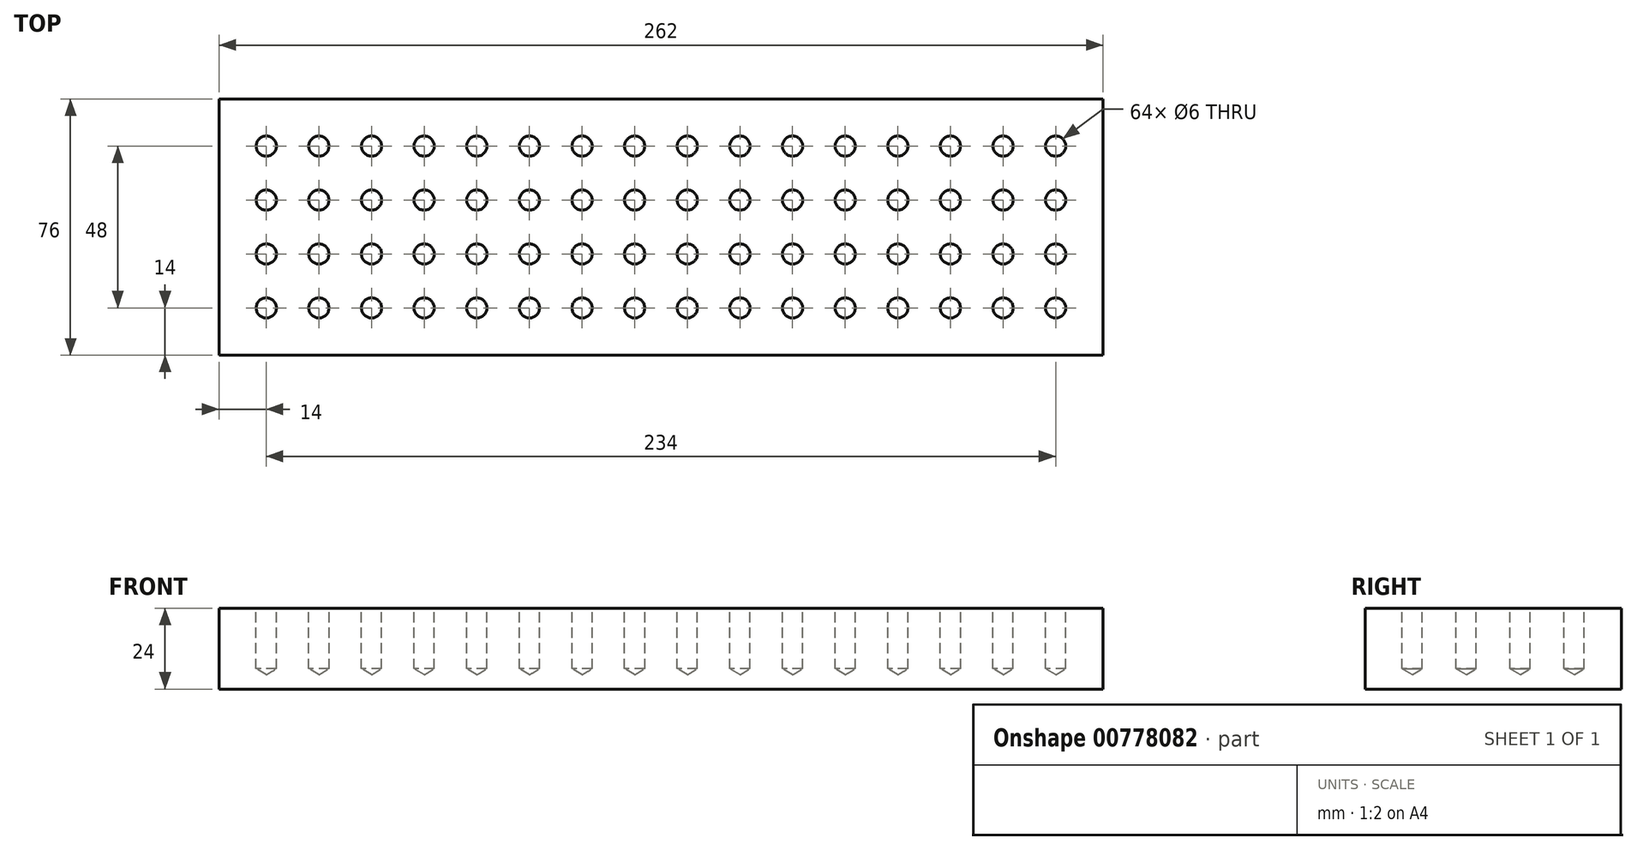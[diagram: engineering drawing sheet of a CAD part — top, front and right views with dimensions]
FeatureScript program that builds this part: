
annotation { "Feature Type Name" : "Feature", "Feature Type Description" : "" }
export const myFeature = defineFeature(function(context is Context, id is Id, definition is map)
    precondition{}
    {
        {
            var Q0;
            Q0=qCreatedBy(makeId("Top.planeOp"),FACE);
            var sketch = newSketch(context, id + "F0", { "sketchPlane" : qUnion([Q0])});
            skLineSegment(sketch, "E0.bottom", {"start": v(-131, 38) * mm, "end": v(131, 38) * mm});
            skLineSegment(sketch, "E0.top", {"start": v(-131, -38) * mm, "end": v(131, -38) * mm});
            skLineSegment(sketch, "E0.left", {"start": v(-131, 38) * mm, "end": v(-131, -38) * mm});
            skLineSegment(sketch, "E0.right", {"start": v(131, 38) * mm, "end": v(131, -38) * mm});
            skPoint(sketch, "E1", {"position": v(-131, 0) * mm});
            skPoint(sketch, "E2", {"position": v(0, 38) * mm});
            skPoint(sketch, "E3", {"position": v(-117, -24) * mm});
            skPoint(sketch, "E4.0.1.0", {"position": v(-117, -8) * mm});
            skPoint(sketch, "E4.0.2.0", {"position": v(-117, 8) * mm});
            skPoint(sketch, "E4.0.3.0", {"position": v(-117, 24) * mm});
            skPoint(sketch, "E4.1.0.0", {"position": v(-101.4, -24) * mm});
            skPoint(sketch, "E4.1.1.0", {"position": v(-101.4, -8) * mm});
            skPoint(sketch, "E4.1.2.0", {"position": v(-101.4, 8) * mm});
            skPoint(sketch, "E4.1.3.0", {"position": v(-101.4, 24) * mm});
            skPoint(sketch, "E4.2.0.0", {"position": v(-85.8, -24) * mm});
            skPoint(sketch, "E4.2.1.0", {"position": v(-85.8, -8) * mm});
            skPoint(sketch, "E4.2.2.0", {"position": v(-85.8, 8) * mm});
            skPoint(sketch, "E4.2.3.0", {"position": v(-85.8, 24) * mm});
            skPoint(sketch, "E4.3.0.0", {"position": v(-70.2, -24) * mm});
            skPoint(sketch, "E4.3.1.0", {"position": v(-70.2, -8) * mm});
            skPoint(sketch, "E4.3.2.0", {"position": v(-70.2, 8) * mm});
            skPoint(sketch, "E4.3.3.0", {"position": v(-70.2, 24) * mm});
            skPoint(sketch, "E4.4.0.0", {"position": v(-54.6, -24) * mm});
            skPoint(sketch, "E4.4.1.0", {"position": v(-54.6, -8) * mm});
            skPoint(sketch, "E4.4.2.0", {"position": v(-54.6, 8) * mm});
            skPoint(sketch, "E4.4.3.0", {"position": v(-54.6, 24) * mm});
            skPoint(sketch, "E4.5.0.0", {"position": v(-39, -24) * mm});
            skPoint(sketch, "E4.5.1.0", {"position": v(-39, -8) * mm});
            skPoint(sketch, "E4.5.2.0", {"position": v(-39, 8) * mm});
            skPoint(sketch, "E4.5.3.0", {"position": v(-39, 24) * mm});
            skPoint(sketch, "E4.6.0.0", {"position": v(-23.4, -24) * mm});
            skPoint(sketch, "E4.6.1.0", {"position": v(-23.4, -8) * mm});
            skPoint(sketch, "E4.6.2.0", {"position": v(-23.4, 8) * mm});
            skPoint(sketch, "E4.6.3.0", {"position": v(-23.4, 24) * mm});
            skPoint(sketch, "E4.7.0.0", {"position": v(-7.8, -24) * mm});
            skPoint(sketch, "E4.7.1.0", {"position": v(-7.8, -8) * mm});
            skPoint(sketch, "E4.7.2.0", {"position": v(-7.8, 8) * mm});
            skPoint(sketch, "E4.7.3.0", {"position": v(-7.8, 24) * mm});
            skPoint(sketch, "E4.8.0.0", {"position": v(7.8, -24) * mm});
            skPoint(sketch, "E4.8.1.0", {"position": v(7.8, -8) * mm});
            skPoint(sketch, "E4.8.2.0", {"position": v(7.8, 8) * mm});
            skPoint(sketch, "E4.8.3.0", {"position": v(7.8, 24) * mm});
            skPoint(sketch, "E4.9.0.0", {"position": v(23.4, -24) * mm});
            skPoint(sketch, "E4.9.1.0", {"position": v(23.4, -8) * mm});
            skPoint(sketch, "E4.9.2.0", {"position": v(23.4, 8) * mm});
            skPoint(sketch, "E4.9.3.0", {"position": v(23.4, 24) * mm});
            skPoint(sketch, "E4.10.0.0", {"position": v(39, -24) * mm});
            skPoint(sketch, "E4.10.1.0", {"position": v(39, -8) * mm});
            skPoint(sketch, "E4.10.2.0", {"position": v(39, 8) * mm});
            skPoint(sketch, "E4.10.3.0", {"position": v(39, 24) * mm});
            skPoint(sketch, "E4.11.0.0", {"position": v(54.6, -24) * mm});
            skPoint(sketch, "E4.11.1.0", {"position": v(54.6, -8) * mm});
            skPoint(sketch, "E4.11.2.0", {"position": v(54.6, 8) * mm});
            skPoint(sketch, "E4.11.3.0", {"position": v(54.6, 24) * mm});
            skPoint(sketch, "E4.12.0.0", {"position": v(70.2, -24) * mm});
            skPoint(sketch, "E4.12.1.0", {"position": v(70.2, -8) * mm});
            skPoint(sketch, "E4.12.2.0", {"position": v(70.2, 8) * mm});
            skPoint(sketch, "E4.12.3.0", {"position": v(70.2, 24) * mm});
            skLineSegment(sketch, "E4.direction1", {"start": v(-117, -24) * mm, "end": v(-101.4, -24) * mm, "construction": true});
            skLineSegment(sketch, "E4.direction2", {"start": v(-117, -24) * mm, "end": v(-117, -8) * mm, "construction": true});
            skPoint(sketch, "E5.0.13.0", {"position": v(85.8, -24) * mm});
            skPoint(sketch, "E5.0.13.1", {"position": v(85.8, -8) * mm});
            skPoint(sketch, "E5.0.13.2", {"position": v(85.8, 8) * mm});
            skPoint(sketch, "E5.0.13.3", {"position": v(85.8, 24) * mm});
            skPoint(sketch, "E5.0.14.0", {"position": v(101.4, -24) * mm});
            skPoint(sketch, "E5.0.14.1", {"position": v(101.4, -8) * mm});
            skPoint(sketch, "E5.0.14.2", {"position": v(101.4, 8) * mm});
            skPoint(sketch, "E5.0.14.3", {"position": v(101.4, 24) * mm});
            skPoint(sketch, "E6.0.15.0", {"position": v(117, -24) * mm});
            skPoint(sketch, "E6.0.15.1", {"position": v(117, -8) * mm});
            skPoint(sketch, "E6.0.15.2", {"position": v(117, 8) * mm});
            skPoint(sketch, "E6.0.15.3", {"position": v(117, 24) * mm});
            skSolve(sketch);
        }
        {
            var Q0;
            Q0=makeQuery(id+"F0.imprint","IMPRINT",FACE,{"disambiguationData":[TD([[makeQuery(id+"F0.imprint","IMPRINT",EDGE,{"derivedFrom":sQuery(id+"F0.wireOp",EDGE,"E0.bottom")}),-1.0]])]});
            extrude(context, id + "F1", {"entities" : qUnion([Q0]), "depth" : 24 * mm, "offsetDistance" : 25 * mm});
        }
        {
            var Q0;
            Q0=makeQuery(id+"F1.opExtrude","CAP_FACE",FACE,{"disambiguationData":[OSD([sQuery(id+"F0.wireOp",EDGE,"E0.bottom"),sQuery(id+"F0.wireOp",EDGE,"E0.top"),sQuery(id+"F0.wireOp",EDGE,"E0.left"),sQuery(id+"F0.wireOp",EDGE,"E0.right")])],"isStart":false});
            var sketch = newSketch(context, id + "F2", { "sketchPlane" : qUnion([Q0])});
            skPoint(sketch, "E7", {"position": v(-117, -24) * mm});
            skCircle(sketch, "E8", {"center": v(-117, -24) * mm, "radius": 3 * mm});
            skCircle(sketch, "E9.0.1.0", {"center": v(-117, -8) * mm, "radius": 3 * mm});
            skPoint(sketch, "E9.0.1.1", {"position": v(-117, -8) * mm});
            skCircle(sketch, "E9.0.2.0", {"center": v(-117, 8) * mm, "radius": 3 * mm});
            skPoint(sketch, "E9.0.2.1", {"position": v(-117, 8) * mm});
            skCircle(sketch, "E9.0.3.0", {"center": v(-117, 24) * mm, "radius": 3 * mm});
            skPoint(sketch, "E9.0.3.1", {"position": v(-117, 24) * mm});
            skCircle(sketch, "E9.1.0.0", {"center": v(-101.4, -24) * mm, "radius": 3 * mm});
            skPoint(sketch, "E9.1.0.1", {"position": v(-101.4, -24) * mm});
            skCircle(sketch, "E9.1.1.0", {"center": v(-101.4, -8) * mm, "radius": 3 * mm});
            skPoint(sketch, "E9.1.1.1", {"position": v(-101.4, -8) * mm});
            skCircle(sketch, "E9.1.2.0", {"center": v(-101.4, 8) * mm, "radius": 3 * mm});
            skPoint(sketch, "E9.1.2.1", {"position": v(-101.4, 8) * mm});
            skCircle(sketch, "E9.1.3.0", {"center": v(-101.4, 24) * mm, "radius": 3 * mm});
            skPoint(sketch, "E9.1.3.1", {"position": v(-101.4, 24) * mm});
            skCircle(sketch, "E9.2.0.0", {"center": v(-85.8, -24) * mm, "radius": 3 * mm});
            skPoint(sketch, "E9.2.0.1", {"position": v(-85.8, -24) * mm});
            skCircle(sketch, "E9.2.1.0", {"center": v(-85.8, -8) * mm, "radius": 3 * mm});
            skPoint(sketch, "E9.2.1.1", {"position": v(-85.8, -8) * mm});
            skCircle(sketch, "E9.2.2.0", {"center": v(-85.8, 8) * mm, "radius": 3 * mm});
            skPoint(sketch, "E9.2.2.1", {"position": v(-85.8, 8) * mm});
            skCircle(sketch, "E9.2.3.0", {"center": v(-85.8, 24) * mm, "radius": 3 * mm});
            skPoint(sketch, "E9.2.3.1", {"position": v(-85.8, 24) * mm});
            skCircle(sketch, "E9.3.0.0", {"center": v(-70.2, -24) * mm, "radius": 3 * mm});
            skPoint(sketch, "E9.3.0.1", {"position": v(-70.2, -24) * mm});
            skCircle(sketch, "E9.3.1.0", {"center": v(-70.2, -8) * mm, "radius": 3 * mm});
            skPoint(sketch, "E9.3.1.1", {"position": v(-70.2, -8) * mm});
            skCircle(sketch, "E9.3.2.0", {"center": v(-70.2, 8) * mm, "radius": 3 * mm});
            skPoint(sketch, "E9.3.2.1", {"position": v(-70.2, 8) * mm});
            skCircle(sketch, "E9.3.3.0", {"center": v(-70.2, 24) * mm, "radius": 3 * mm});
            skPoint(sketch, "E9.3.3.1", {"position": v(-70.2, 24) * mm});
            skCircle(sketch, "E9.4.0.0", {"center": v(-54.6, -24) * mm, "radius": 3 * mm});
            skPoint(sketch, "E9.4.0.1", {"position": v(-54.6, -24) * mm});
            skCircle(sketch, "E9.4.1.0", {"center": v(-54.6, -8) * mm, "radius": 3 * mm});
            skPoint(sketch, "E9.4.1.1", {"position": v(-54.6, -8) * mm});
            skCircle(sketch, "E9.4.2.0", {"center": v(-54.6, 8) * mm, "radius": 3 * mm});
            skPoint(sketch, "E9.4.2.1", {"position": v(-54.6, 8) * mm});
            skCircle(sketch, "E9.4.3.0", {"center": v(-54.6, 24) * mm, "radius": 3 * mm});
            skPoint(sketch, "E9.4.3.1", {"position": v(-54.6, 24) * mm});
            skCircle(sketch, "E9.5.0.0", {"center": v(-39, -24) * mm, "radius": 3 * mm});
            skPoint(sketch, "E9.5.0.1", {"position": v(-39, -24) * mm});
            skCircle(sketch, "E9.5.1.0", {"center": v(-39, -8) * mm, "radius": 3 * mm});
            skPoint(sketch, "E9.5.1.1", {"position": v(-39, -8) * mm});
            skCircle(sketch, "E9.5.2.0", {"center": v(-39, 8) * mm, "radius": 3 * mm});
            skPoint(sketch, "E9.5.2.1", {"position": v(-39, 8) * mm});
            skCircle(sketch, "E9.5.3.0", {"center": v(-39, 24) * mm, "radius": 3 * mm});
            skPoint(sketch, "E9.5.3.1", {"position": v(-39, 24) * mm});
            skCircle(sketch, "E9.6.0.0", {"center": v(-23.4, -24) * mm, "radius": 3 * mm});
            skPoint(sketch, "E9.6.0.1", {"position": v(-23.4, -24) * mm});
            skCircle(sketch, "E9.6.1.0", {"center": v(-23.4, -8) * mm, "radius": 3 * mm});
            skPoint(sketch, "E9.6.1.1", {"position": v(-23.4, -8) * mm});
            skCircle(sketch, "E9.6.2.0", {"center": v(-23.4, 8) * mm, "radius": 3 * mm});
            skPoint(sketch, "E9.6.2.1", {"position": v(-23.4, 8) * mm});
            skCircle(sketch, "E9.6.3.0", {"center": v(-23.4, 24) * mm, "radius": 3 * mm});
            skPoint(sketch, "E9.6.3.1", {"position": v(-23.4, 24) * mm});
            skCircle(sketch, "E9.7.0.0", {"center": v(-7.8, -24) * mm, "radius": 3 * mm});
            skPoint(sketch, "E9.7.0.1", {"position": v(-7.8, -24) * mm});
            skCircle(sketch, "E9.7.1.0", {"center": v(-7.8, -8) * mm, "radius": 3 * mm});
            skPoint(sketch, "E9.7.1.1", {"position": v(-7.8, -8) * mm});
            skCircle(sketch, "E9.7.2.0", {"center": v(-7.8, 8) * mm, "radius": 3 * mm});
            skPoint(sketch, "E9.7.2.1", {"position": v(-7.8, 8) * mm});
            skCircle(sketch, "E9.7.3.0", {"center": v(-7.8, 24) * mm, "radius": 3 * mm});
            skPoint(sketch, "E9.7.3.1", {"position": v(-7.8, 24) * mm});
            skCircle(sketch, "E9.8.0.0", {"center": v(7.8, -24) * mm, "radius": 3 * mm});
            skPoint(sketch, "E9.8.0.1", {"position": v(7.8, -24) * mm});
            skCircle(sketch, "E9.8.1.0", {"center": v(7.8, -8) * mm, "radius": 3 * mm});
            skPoint(sketch, "E9.8.1.1", {"position": v(7.8, -8) * mm});
            skCircle(sketch, "E9.8.2.0", {"center": v(7.8, 8) * mm, "radius": 3 * mm});
            skPoint(sketch, "E9.8.2.1", {"position": v(7.8, 8) * mm});
            skCircle(sketch, "E9.8.3.0", {"center": v(7.8, 24) * mm, "radius": 3 * mm});
            skPoint(sketch, "E9.8.3.1", {"position": v(7.8, 24) * mm});
            skCircle(sketch, "E9.9.0.0", {"center": v(23.4, -24) * mm, "radius": 3 * mm});
            skPoint(sketch, "E9.9.0.1", {"position": v(23.4, -24) * mm});
            skCircle(sketch, "E9.9.1.0", {"center": v(23.4, -8) * mm, "radius": 3 * mm});
            skPoint(sketch, "E9.9.1.1", {"position": v(23.4, -8) * mm});
            skCircle(sketch, "E9.9.2.0", {"center": v(23.4, 8) * mm, "radius": 3 * mm});
            skPoint(sketch, "E9.9.2.1", {"position": v(23.4, 8) * mm});
            skCircle(sketch, "E9.9.3.0", {"center": v(23.4, 24) * mm, "radius": 3 * mm});
            skPoint(sketch, "E9.9.3.1", {"position": v(23.4, 24) * mm});
            skCircle(sketch, "E9.10.0.0", {"center": v(39, -24) * mm, "radius": 3 * mm});
            skPoint(sketch, "E9.10.0.1", {"position": v(39, -24) * mm});
            skCircle(sketch, "E9.10.1.0", {"center": v(39, -8) * mm, "radius": 3 * mm});
            skPoint(sketch, "E9.10.1.1", {"position": v(39, -8) * mm});
            skCircle(sketch, "E9.10.2.0", {"center": v(39, 8) * mm, "radius": 3 * mm});
            skPoint(sketch, "E9.10.2.1", {"position": v(39, 8) * mm});
            skCircle(sketch, "E9.10.3.0", {"center": v(39, 24) * mm, "radius": 3 * mm});
            skPoint(sketch, "E9.10.3.1", {"position": v(39, 24) * mm});
            skCircle(sketch, "E9.11.0.0", {"center": v(54.6, -24) * mm, "radius": 3 * mm});
            skPoint(sketch, "E9.11.0.1", {"position": v(54.6, -24) * mm});
            skCircle(sketch, "E9.11.1.0", {"center": v(54.6, -8) * mm, "radius": 3 * mm});
            skPoint(sketch, "E9.11.1.1", {"position": v(54.6, -8) * mm});
            skCircle(sketch, "E9.11.2.0", {"center": v(54.6, 8) * mm, "radius": 3 * mm});
            skPoint(sketch, "E9.11.2.1", {"position": v(54.6, 8) * mm});
            skCircle(sketch, "E9.11.3.0", {"center": v(54.6, 24) * mm, "radius": 3 * mm});
            skPoint(sketch, "E9.11.3.1", {"position": v(54.6, 24) * mm});
            skCircle(sketch, "E9.12.0.0", {"center": v(70.2, -24) * mm, "radius": 3 * mm});
            skPoint(sketch, "E9.12.0.1", {"position": v(70.2, -24) * mm});
            skCircle(sketch, "E9.12.1.0", {"center": v(70.2, -8) * mm, "radius": 3 * mm});
            skPoint(sketch, "E9.12.1.1", {"position": v(70.2, -8) * mm});
            skCircle(sketch, "E9.12.2.0", {"center": v(70.2, 8) * mm, "radius": 3 * mm});
            skPoint(sketch, "E9.12.2.1", {"position": v(70.2, 8) * mm});
            skCircle(sketch, "E9.12.3.0", {"center": v(70.2, 24) * mm, "radius": 3 * mm});
            skPoint(sketch, "E9.12.3.1", {"position": v(70.2, 24) * mm});
            skLineSegment(sketch, "E9.direction1", {"start": v(-117, -24) * mm, "end": v(-101.4, -24) * mm, "construction": true});
            skLineSegment(sketch, "E9.direction2", {"start": v(-117, -24) * mm, "end": v(-117, -8) * mm, "construction": true});
            skLineSegment(sketch, "E10.bottom", {"start": v(-131, 38) * mm, "end": v(131, 38) * mm});
            skLineSegment(sketch, "E10.top", {"start": v(-131, -38) * mm, "end": v(131, -38) * mm});
            skLineSegment(sketch, "E10.left", {"start": v(-131, 38) * mm, "end": v(-131, -38) * mm});
            skLineSegment(sketch, "E10.right", {"start": v(131, 38) * mm, "end": v(131, -38) * mm});
            skCircle(sketch, "E11.0.13.0", {"center": v(85.8, -24) * mm, "radius": 3 * mm});
            skPoint(sketch, "E11.2.13.0", {"position": v(85.8, -24) * mm});
            skCircle(sketch, "E11.0.13.1", {"center": v(85.8, -8) * mm, "radius": 3 * mm});
            skPoint(sketch, "E11.2.13.1", {"position": v(85.8, -8) * mm});
            skCircle(sketch, "E11.0.13.2", {"center": v(85.8, 8) * mm, "radius": 3 * mm});
            skPoint(sketch, "E11.2.13.2", {"position": v(85.8, 8) * mm});
            skCircle(sketch, "E11.0.13.3", {"center": v(85.8, 24) * mm, "radius": 3 * mm});
            skPoint(sketch, "E11.2.13.3", {"position": v(85.8, 24) * mm});
            skCircle(sketch, "E11.0.14.0", {"center": v(101.4, -24) * mm, "radius": 3 * mm});
            skPoint(sketch, "E11.2.14.0", {"position": v(101.4, -24) * mm});
            skCircle(sketch, "E11.0.14.1", {"center": v(101.4, -8) * mm, "radius": 3 * mm});
            skPoint(sketch, "E11.2.14.1", {"position": v(101.4, -8) * mm});
            skCircle(sketch, "E11.0.14.2", {"center": v(101.4, 8) * mm, "radius": 3 * mm});
            skPoint(sketch, "E11.2.14.2", {"position": v(101.4, 8) * mm});
            skCircle(sketch, "E11.0.14.3", {"center": v(101.4, 24) * mm, "radius": 3 * mm});
            skPoint(sketch, "E11.2.14.3", {"position": v(101.4, 24) * mm});
            skCircle(sketch, "E11.0.15.0", {"center": v(117, -24) * mm, "radius": 3 * mm});
            skPoint(sketch, "E11.2.15.0", {"position": v(117, -24) * mm});
            skCircle(sketch, "E11.0.15.1", {"center": v(117, -8) * mm, "radius": 3 * mm});
            skPoint(sketch, "E11.2.15.1", {"position": v(117, -8) * mm});
            skCircle(sketch, "E11.0.15.2", {"center": v(117, 8) * mm, "radius": 3 * mm});
            skPoint(sketch, "E11.2.15.2", {"position": v(117, 8) * mm});
            skCircle(sketch, "E11.0.15.3", {"center": v(117, 24) * mm, "radius": 3 * mm});
            skPoint(sketch, "E11.2.15.3", {"position": v(117, 24) * mm});
            skSolve(sketch);
        }
        {
            var Q0;
            Q0=sQuery(id+"F2.wireOp",VERTEX,"E9.0.3.1");
            var Q1;
            Q1=sQuery(id+"F2.wireOp",VERTEX,"E9.0.2.1");
            var Q2;
            Q2=sQuery(id+"F2.wireOp",VERTEX,"E9.0.1.1");
            var Q3;
            Q3=sQuery(id+"F2.wireOp",VERTEX,"E7");
            var Q4;
            Q4=sQuery(id+"F2.wireOp",VERTEX,"E9.1.3.1");
            var Q5;
            Q5=sQuery(id+"F2.wireOp",VERTEX,"E9.1.2.0.center");
            var Q6;
            Q6=sQuery(id+"F2.wireOp",VERTEX,"E9.1.1.0.center");
            var Q7;
            Q7=sQuery(id+"F2.wireOp",VERTEX,"E9.1.0.1");
            var Q8;
            Q8=sQuery(id+"F2.wireOp",VERTEX,"E9.4.2.0.center");
            var Q9;
            Q9=sQuery(id+"F2.wireOp",VERTEX,"E9.9.3.1");
            var Q10;
            Q10=sQuery(id+"F2.wireOp",VERTEX,"E9.6.1.1");
            var Q11;
            Q11=sQuery(id+"F2.wireOp",VERTEX,"E9.2.1.0.center");
            var Q12;
            Q12=sQuery(id+"F2.wireOp",VERTEX,"E9.6.2.0.center");
            var Q13;
            Q13=sQuery(id+"F2.wireOp",VERTEX,"E9.11.0.1");
            var Q14;
            Q14=sQuery(id+"F2.wireOp",VERTEX,"E9.3.0.1");
            var Q15;
            Q15=sQuery(id+"F2.wireOp",VERTEX,"E9.5.3.0.center");
            var Q16;
            Q16=sQuery(id+"F2.wireOp",VERTEX,"E9.3.3.1");
            var Q17;
            Q17=sQuery(id+"F2.wireOp",VERTEX,"E9.8.1.0.center");
            var Q18;
            Q18=sQuery(id+"F2.wireOp",VERTEX,"E9.3.1.0.center");
            var Q19;
            Q19=sQuery(id+"F2.wireOp",VERTEX,"E9.10.2.1");
            var Q20;
            Q20=sQuery(id+"F2.wireOp",VERTEX,"E9.5.0.1");
            var Q21;
            Q21=sQuery(id+"F2.wireOp",VERTEX,"E9.7.3.0.center");
            var Q22;
            Q22=sQuery(id+"F2.wireOp",VERTEX,"E9.12.2.1");
            var Q23;
            Q23=sQuery(id+"F2.wireOp",VERTEX,"E9.7.2.1");
            var Q24;
            Q24=sQuery(id+"F2.wireOp",VERTEX,"E9.11.2.0.center");
            var Q25;
            Q25=sQuery(id+"F2.wireOp",VERTEX,"E9.12.0.0.center");
            var Q26;
            Q26=sQuery(id+"F2.wireOp",VERTEX,"E9.6.0.0.center");
            var Q27;
            Q27=sQuery(id+"F2.wireOp",VERTEX,"E9.8.3.0.center");
            var Q28;
            Q28=sQuery(id+"F2.wireOp",VERTEX,"E9.4.3.0.center");
            var Q29;
            Q29=sQuery(id+"F2.wireOp",VERTEX,"E9.7.0.1");
            var Q30;
            Q30=sQuery(id+"F2.wireOp",VERTEX,"E9.7.1.1");
            var Q31;
            Q31=sQuery(id+"F2.wireOp",VERTEX,"E9.4.0.1");
            var Q32;
            Q32=sQuery(id+"F2.wireOp",VERTEX,"E9.5.2.1");
            var Q33;
            Q33=sQuery(id+"F2.wireOp",VERTEX,"E9.10.3.0.center");
            var Q34;
            Q34=sQuery(id+"F2.wireOp",VERTEX,"E9.9.0.1");
            var Q35;
            Q35=sQuery(id+"F2.wireOp",VERTEX,"E9.5.1.1");
            var Q36;
            Q36=sQuery(id+"F2.wireOp",VERTEX,"E9.11.3.0.center");
            var Q37;
            Q37=sQuery(id+"F2.wireOp",VERTEX,"E9.4.1.1");
            var Q38;
            Q38=sQuery(id+"F2.wireOp",VERTEX,"E9.10.1.0.center");
            var Q39;
            Q39=sQuery(id+"F2.wireOp",VERTEX,"E9.2.0.1");
            var Q40;
            Q40=sQuery(id+"F2.wireOp",VERTEX,"E9.11.1.1");
            var Q41;
            Q41=sQuery(id+"F2.wireOp",VERTEX,"E9.12.3.1");
            var Q42;
            Q42=sQuery(id+"F2.wireOp",VERTEX,"E9.3.2.1");
            var Q43;
            Q43=sQuery(id+"F2.wireOp",VERTEX,"E9.9.2.1");
            var Q44;
            Q44=sQuery(id+"F2.wireOp",VERTEX,"E9.12.1.1");
            var Q45;
            Q45=sQuery(id+"F2.wireOp",VERTEX,"E9.2.3.1");
            var Q46;
            Q46=sQuery(id+"F2.wireOp",VERTEX,"E9.6.3.1");
            var Q47;
            Q47=sQuery(id+"F2.wireOp",VERTEX,"E9.2.2.0.center");
            var Q48;
            Q48=sQuery(id+"F2.wireOp",VERTEX,"E9.8.0.0.center");
            var Q49;
            Q49=sQuery(id+"F2.wireOp",VERTEX,"E9.9.1.1");
            var Q50;
            Q50=sQuery(id+"F2.wireOp",VERTEX,"E9.8.2.1");
            var Q51;
            Q51=sQuery(id+"F2.wireOp",VERTEX,"E9.10.0.1");
            var Q52;
            Q52=sQuery(id+"F2.wireOp",VERTEX,"E11.2.14.2");
            var Q53;
            Q53=sQuery(id+"F2.wireOp",VERTEX,"E11.0.15.2.center");
            var Q54;
            Q54=sQuery(id+"F2.wireOp",VERTEX,"E11.0.13.3.center");
            var Q55;
            Q55=sQuery(id+"F2.wireOp",VERTEX,"E11.2.13.1");
            var Q56;
            Q56=sQuery(id+"F2.wireOp",VERTEX,"E11.0.14.1.center");
            var Q57;
            Q57=sQuery(id+"F2.wireOp",VERTEX,"E11.2.14.0");
            var Q58;
            Q58=sQuery(id+"F2.wireOp",VERTEX,"E11.0.15.1.center");
            var Q59;
            Q59=sQuery(id+"F2.wireOp",VERTEX,"E11.0.15.3.center");
            var Q60;
            Q60=sQuery(id+"F2.wireOp",VERTEX,"E11.2.13.0");
            var Q61;
            Q61=sQuery(id+"F2.wireOp",VERTEX,"E11.2.15.0");
            var Q62;
            Q62=sQuery(id+"F2.wireOp",VERTEX,"E11.0.13.2.center");
            var Q63;
            Q63=sQuery(id+"F2.wireOp",VERTEX,"E11.0.14.3.center");
            var Q64;
            Q64=makeQuery(id+"F1.opExtrude","SWEPT_BODY",BODY,{"disambiguationData":[OSD([sQuery(id+"F0.wireOp",EDGE,"E0.bottom"),sQuery(id+"F0.wireOp",EDGE,"E0.top"),sQuery(id+"F0.wireOp",EDGE,"E0.left"),sQuery(id+"F0.wireOp",EDGE,"E0.right")])]});
            hole(context, id + "F3", {"style" : HoleStyle.SIMPLE, "endStyle" : HoleEndStyle.BLIND, "holeDiameter" : 6 * mm, "majorDiameter" : 5 * mm, "holeDepth" : 18 * mm, "isTappedThrough" : true, "tappedDepth" : 12 * mm, "tapClearance" : 3, "locations" : qUnion([Q0, Q1, Q2, Q3, Q4, Q5, Q6, Q7, Q8, Q9, Q10, Q11, Q12, Q13, Q14, Q15, Q16, Q17, Q18, Q19, Q20, Q21, Q22, Q23, Q24, Q25, Q26, Q27, Q28, Q29, Q30, Q31, Q32, Q33, Q34, Q35, Q36, Q37, Q38, Q39, Q40, Q41, Q42, Q43, Q44, Q45, Q46, Q47, Q48, Q49, Q50, Q51, Q52, Q53, Q54, Q55, Q56, Q57, Q58, Q59, Q60, Q61, Q62, Q63]), "scope" : qUnion([Q64])});
        }
    });
